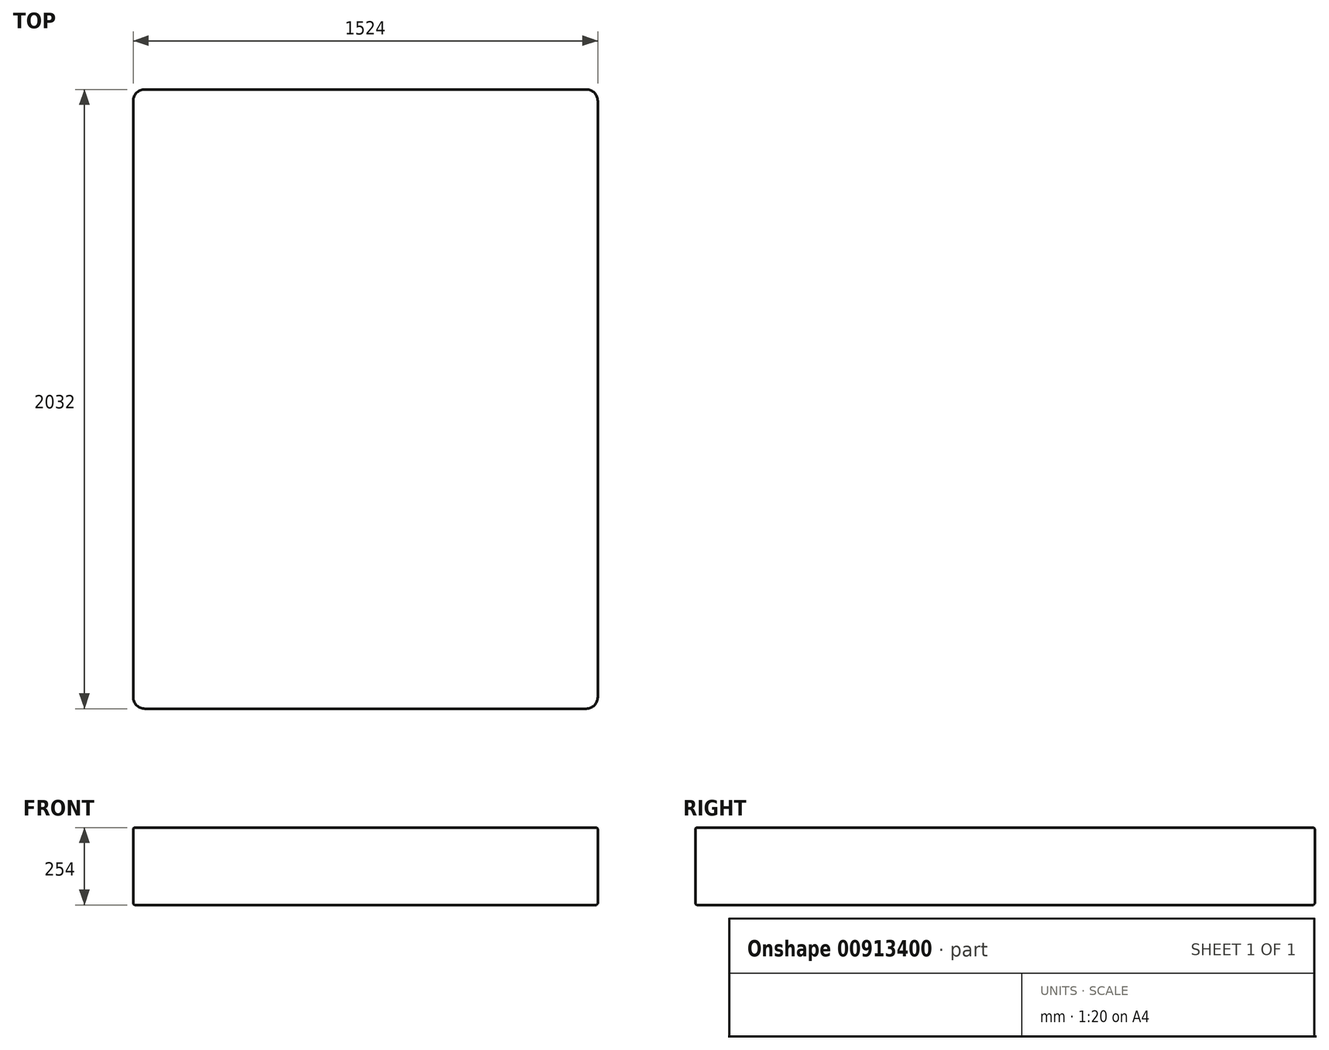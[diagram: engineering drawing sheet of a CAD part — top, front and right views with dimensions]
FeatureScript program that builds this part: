
annotation { "Feature Type Name" : "Feature", "Feature Type Description" : "" }
export const myFeature = defineFeature(function(context is Context, id is Id, definition is map)
    precondition{}
    {
        {
            var Q0;
            Q0=qCreatedBy(makeId("Top.planeOp"),FACE);
            var sketch = newSketch(context, id + "F0", { "sketchPlane" : qUnion([Q0])});
            skLineSegment(sketch, "E0.bottom", {"start": v(762, 1016) * mm, "end": v(-762, 1016) * mm});
            skLineSegment(sketch, "E0.top", {"start": v(762, -1016) * mm, "end": v(-762, -1016) * mm});
            skLineSegment(sketch, "E0.left", {"start": v(762, 1016) * mm, "end": v(762, -1016) * mm});
            skLineSegment(sketch, "E0.right", {"start": v(-762, 1016) * mm, "end": v(-762, -1016) * mm});
            skPoint(sketch, "E0.middle", {"position": v(0, 0) * mm});
            skSolve(sketch);
        }
        {
            var Q0;
            Q0 = qSketchRegion(id + "F0", true);
            extrude(context, id + "F1", {"entities" : qUnion([Q0]), "depth" : 254 * mm, "offsetDistance" : 25.4 * mm});
        }
        {
            var Q0;
            Q0=makeQuery(id+"F1.opExtrude","SWEPT_EDGE",EDGE,{"disambiguationData":[OSD([sQuery(id+"F0.wireOp",EDGE,"E0.top"),sQuery(id+"F0.wireOp",EDGE,"E0.right")])]});
            var Q1;
            Q1=makeQuery(id+"F1.opExtrude","SWEPT_EDGE",EDGE,{"disambiguationData":[OSD([sQuery(id+"F0.wireOp",EDGE,"E0.top"),sQuery(id+"F0.wireOp",EDGE,"E0.left")])]});
            var Q2;
            Q2=makeQuery(id+"F1.opExtrude","SWEPT_EDGE",EDGE,{"disambiguationData":[OSD([sQuery(id+"F0.wireOp",EDGE,"E0.bottom"),sQuery(id+"F0.wireOp",EDGE,"E0.left")])]});
            var Q3;
            Q3=makeQuery(id+"F1.opExtrude","SWEPT_EDGE",EDGE,{"disambiguationData":[OSD([sQuery(id+"F0.wireOp",EDGE,"E0.bottom"),sQuery(id+"F0.wireOp",EDGE,"E0.right")])]});
            fillet(context, id + "F2", {"entities" : qUnion([Q0, Q1, Q2, Q3]), "radius" : 38.1 * mm, "tangentPropagation" : true, "allowEdgeOverflow" : false});
        }
        {
            var Q0;
            Q0=makeQuery(id+"F1.opExtrude","CAP_EDGE",EDGE,{"disambiguationData":[OSD([sQuery(id+"F0.wireOp",EDGE,"E0.top")])],"isStart":false});
            var Q1;
            Q1=makeQuery(id+"F1.opExtrude","CAP_EDGE",EDGE,{"disambiguationData":[OSD([sQuery(id+"F0.wireOp",EDGE,"E0.top")])],"isStart":true});
            fillet(context, id + "F3", {"entities" : qUnion([Q0, Q1]), "radius" : 6.35 * mm, "tangentPropagation" : true, "allowEdgeOverflow" : false});
        }
    });
